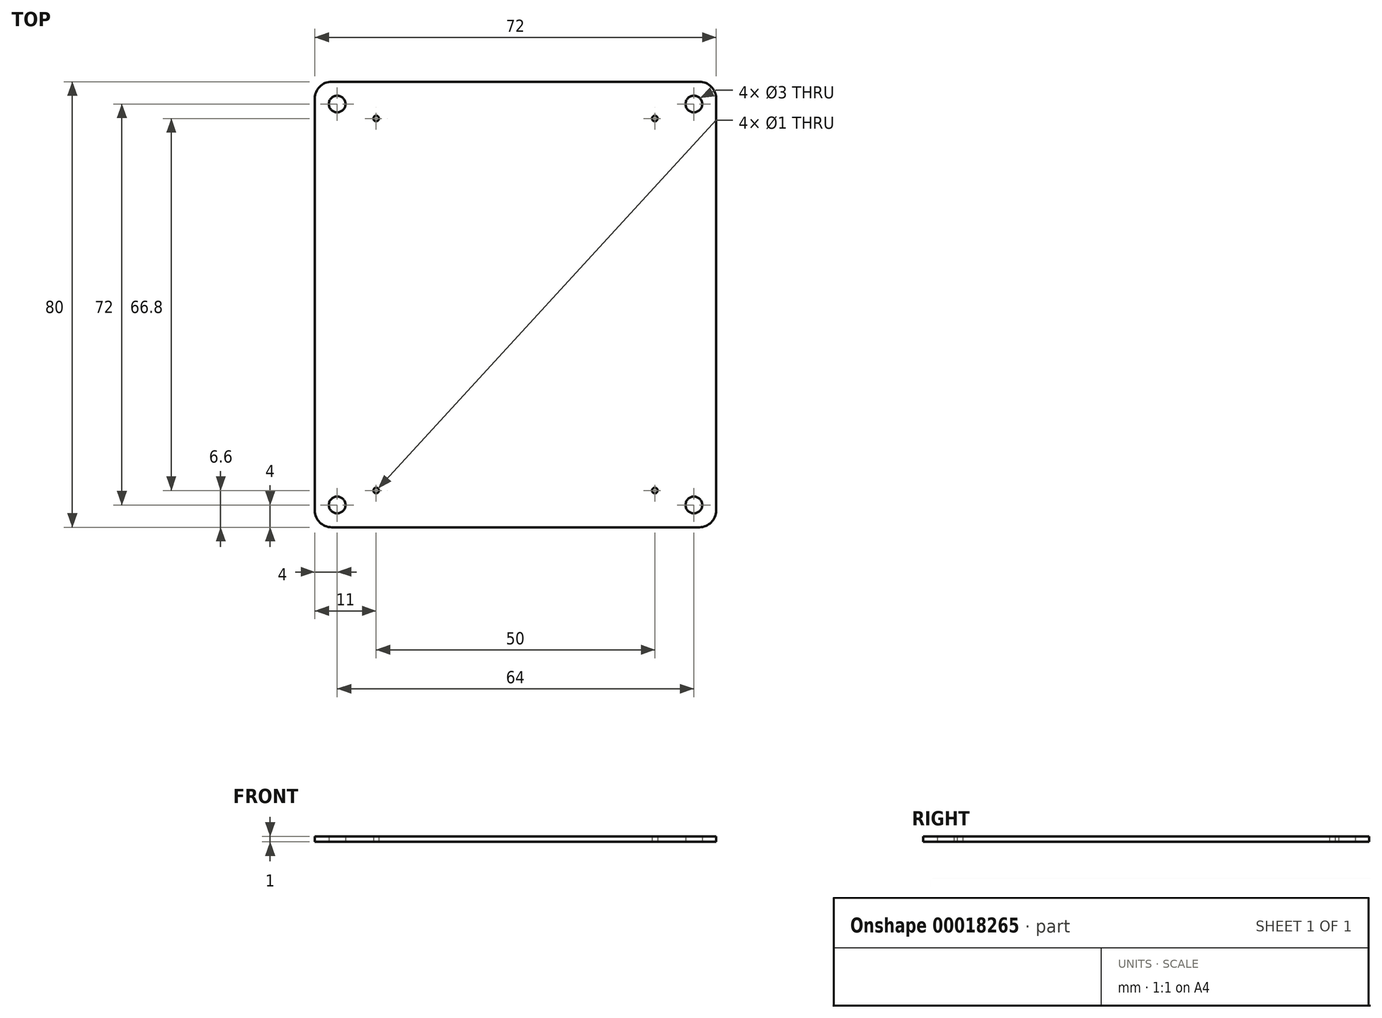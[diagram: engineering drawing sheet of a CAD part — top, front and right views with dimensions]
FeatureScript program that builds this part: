
annotation { "Feature Type Name" : "Feature", "Feature Type Description" : "" }
export const myFeature = defineFeature(function(context is Context, id is Id, definition is map)
    precondition{}
    {
        {
            var Q0;
            Q0=qCreatedBy(makeId("Top.planeOp"),FACE);
            var sketch = newSketch(context, id + "F0", { "sketchPlane" : qUnion([Q0])});
            skLineSegment(sketch, "E0.rect.bottom", {"start": v(33, -40) * mm, "end": v(-33, -40) * mm});
            skLineSegment(sketch, "E0.rect.top", {"start": v(33, 40) * mm, "end": v(-33, 40) * mm});
            skLineSegment(sketch, "E0.rect.left", {"start": v(36, -37) * mm, "end": v(36, 37) * mm});
            skLineSegment(sketch, "E0.rect.right", {"start": v(-36, -37) * mm, "end": v(-36, 37) * mm});
            skPoint(sketch, "E0.rect.middle", {"position": v(0, 0) * mm});
            skPoint(sketch, "E1.visualSharp", {"position": v(-36, 40) * mm});
            skArc(sketch, "E1.filletArc", {"start": v(-33, 40) * mm, "mid": v(-35.12, 39.12) * mm, "end": v(-36, 37) * mm});
            skPoint(sketch, "E2.visualSharp", {"position": v(36, 40) * mm});
            skArc(sketch, "E2.filletArc", {"start": v(36, 37) * mm, "mid": v(35.12, 39.12) * mm, "end": v(33, 40) * mm});
            skPoint(sketch, "E3.visualSharp", {"position": v(36, -40) * mm});
            skArc(sketch, "E3.filletArc", {"start": v(33, -40) * mm, "mid": v(35.12, -39.12) * mm, "end": v(36, -37) * mm});
            skPoint(sketch, "E4.visualSharp", {"position": v(-36, -40) * mm});
            skArc(sketch, "E4.filletArc", {"start": v(-36, -37) * mm, "mid": v(-35.12, -39.12) * mm, "end": v(-33, -40) * mm});
            skLineSegment(sketch, "E5.rect.bottom", {"start": v(32, 36) * mm, "end": v(-32, 36) * mm, "construction": true});
            skLineSegment(sketch, "E5.rect.top", {"start": v(32, -36) * mm, "end": v(-32, -36) * mm, "construction": true});
            skLineSegment(sketch, "E5.rect.left", {"start": v(32, 36) * mm, "end": v(32, -36) * mm, "construction": true});
            skLineSegment(sketch, "E5.rect.right", {"start": v(-32, 36) * mm, "end": v(-32, -36) * mm, "construction": true});
            skCircle(sketch, "E6", {"center": v(32, 36) * mm, "radius": 1.5 * mm});
            skCircle(sketch, "E7", {"center": v(-32, 36) * mm, "radius": 1.5 * mm});
            skCircle(sketch, "E8", {"center": v(-32, -36) * mm, "radius": 1.5 * mm});
            skCircle(sketch, "E9", {"center": v(32, -36) * mm, "radius": 1.5 * mm});
            skSolve(sketch);
        }
        {
            var Q0;
            Q0=makeQuery(id+"F0.imprint","IMPRINT",FACE,{"disambiguationData":[TD([[makeQuery(id+"F0.imprint","IMPRINT",EDGE,{"derivedFrom":sQuery(id+"F0.wireOp",EDGE,"E0.rect.bottom")}),-1.0]])]});
            extrude(context, id + "F1", {"entities" : qUnion([Q0]), "depth" : 1 * mm});
        }
        {
            var Q0;
            Q0=qCreatedBy(makeId("Top.planeOp"),FACE);
            var sketch = newSketch(context, id + "F2", { "sketchPlane" : qUnion([Q0])});
            skLineSegment(sketch, "E10.rect.bottom", {"start": v(25, -33.4) * mm, "end": v(-25, -33.4) * mm, "construction": true});
            skLineSegment(sketch, "E10.rect.top", {"start": v(25, 33.4) * mm, "end": v(-25, 33.4) * mm, "construction": true});
            skLineSegment(sketch, "E10.rect.left", {"start": v(25, -33.4) * mm, "end": v(25, 33.4) * mm, "construction": true});
            skLineSegment(sketch, "E10.rect.right", {"start": v(-25, -33.4) * mm, "end": v(-25, 33.4) * mm, "construction": true});
            skPoint(sketch, "E10.rect.middle", {"position": v(0, 0) * mm});
            skLineSegment(sketch, "E11.0", {"start": v(-30, -38.4) * mm, "end": v(-30, 38.4) * mm, "construction": true});
            skLineSegment(sketch, "E11.1", {"start": v(30, -38.4) * mm, "end": v(-30, -38.4) * mm, "construction": true});
            skLineSegment(sketch, "E11.2", {"start": v(30, -38.4) * mm, "end": v(30, 38.4) * mm, "construction": true});
            skLineSegment(sketch, "E11.3", {"start": v(30, 38.4) * mm, "end": v(-30, 38.4) * mm, "construction": true});
            skCircle(sketch, "E12", {"center": v(-25, 33.4) * mm, "radius": 0.5 * mm});
            skCircle(sketch, "E13", {"center": v(25, 33.4) * mm, "radius": 0.5 * mm});
            skCircle(sketch, "E14", {"center": v(-25, -33.4) * mm, "radius": 0.5 * mm});
            skCircle(sketch, "E15", {"center": v(25, -33.4) * mm, "radius": 0.5 * mm});
            skSolve(sketch);
        }
        {
            var Q0;
            Q0 = qSketchRegion(id + "F2", true);
            extrude(context, id + "F3", {"entities" : qUnion([Q0]), "operationType" : NewBodyOperationType.REMOVE, "endBound" : BoundingType.THROUGH_ALL, "depth" : 25 * mm});
        }
    });
